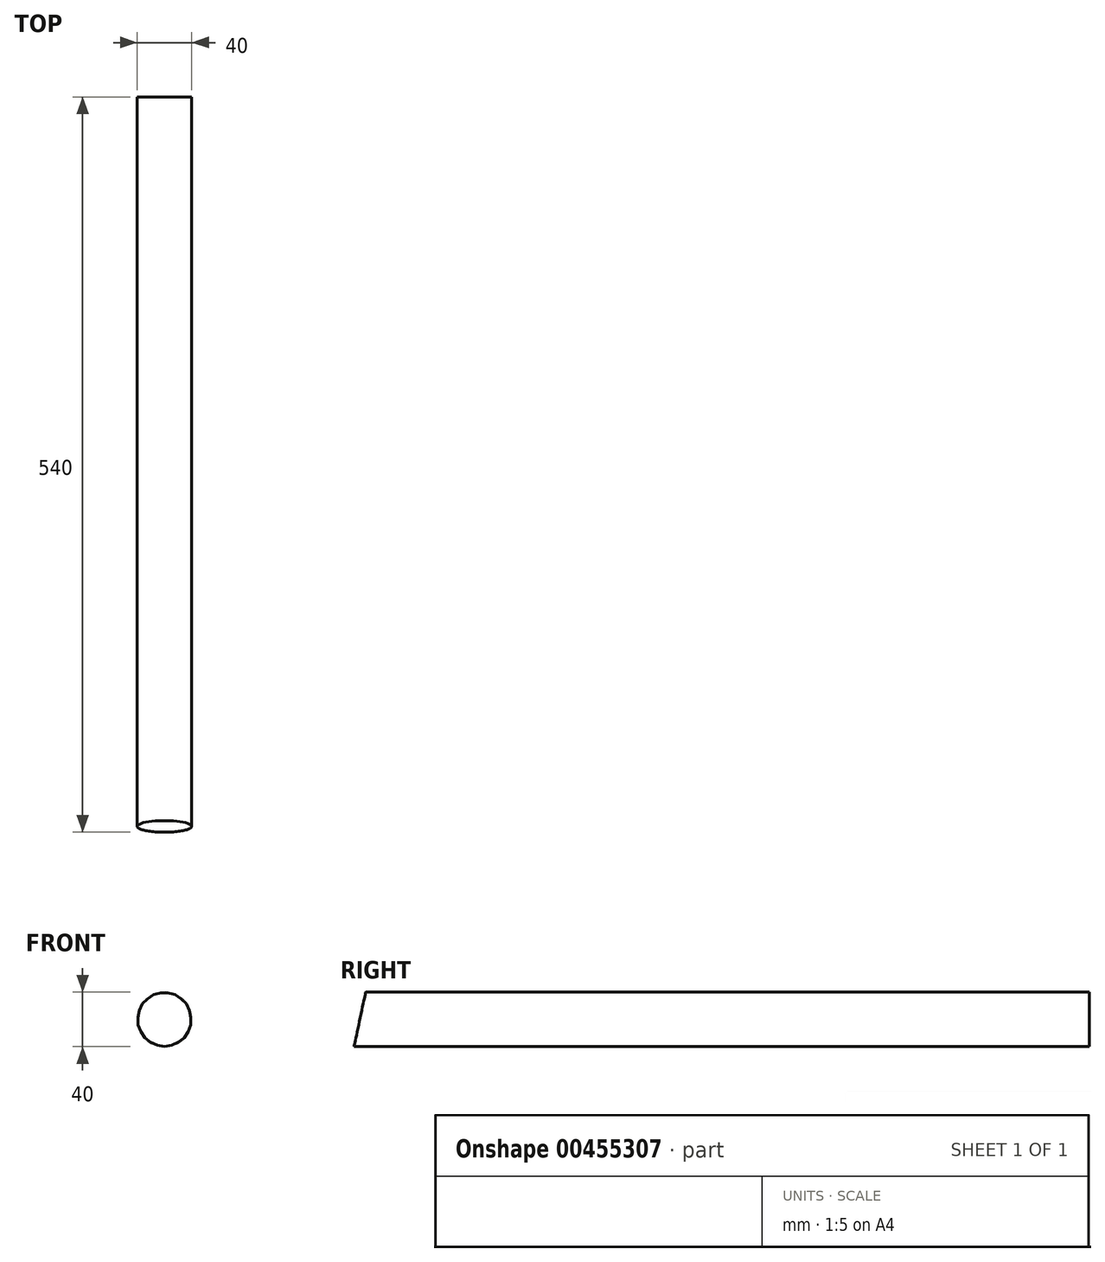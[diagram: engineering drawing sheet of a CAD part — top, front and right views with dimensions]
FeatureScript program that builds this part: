
annotation { "Feature Type Name" : "Feature", "Feature Type Description" : "" }
export const myFeature = defineFeature(function(context is Context, id is Id, definition is map)
    precondition{}
    {
        {
            var Q0;
            Q0=qCreatedBy(makeId("Front.planeOp"),FACE);
            var sketch = newSketch(context, id + "F0", { "sketchPlane" : qUnion([Q0])});
            skCircle(sketch, "E0", {"center": v(0, 0) * mm, "radius": 20 * mm});
            skSolve(sketch);
        }
        {
            var Q0;
            Q0 = qSketchRegion(id + "F0", true);
            extrude(context, id + "F1", {"entities" : qUnion([Q0]), "oppositeDirection" : true, "depth" : 540 * mm, "offsetDistance" : 25 * mm});
        }
        {
            var Q0;
            Q0=qCreatedBy(makeId("Right.planeOp"),FACE);
            var sketch = newSketch(context, id + "F2", { "sketchPlane" : qUnion([Q0])});
            skLineSegment(sketch, "E1", {"start": v(0, -20) * mm, "end": v(8.5, 20) * mm});
            skLineSegment(sketch, "E2.0", {"start": v(0, -20) * mm, "end": v(0, 20) * mm});
            skLineSegment(sketch, "E3", {"start": v(0, 20) * mm, "end": v(8.5, 20) * mm});
            skSolve(sketch);
        }
        {
            var Q0;
            Q0 = qSketchRegion(id + "F2", true);
            extrude(context, id + "F3", {"entities" : qUnion([Q0]), "operationType" : NewBodyOperationType.REMOVE, "oppositeDirection" : true, "depth" : 25 * mm, "offsetDistance" : 25 * mm, "hasSecondDirection" : true, "secondDirectionOppositeDirection" : false, "secondDirectionDepth" : 25 * mm});
        }
    });
